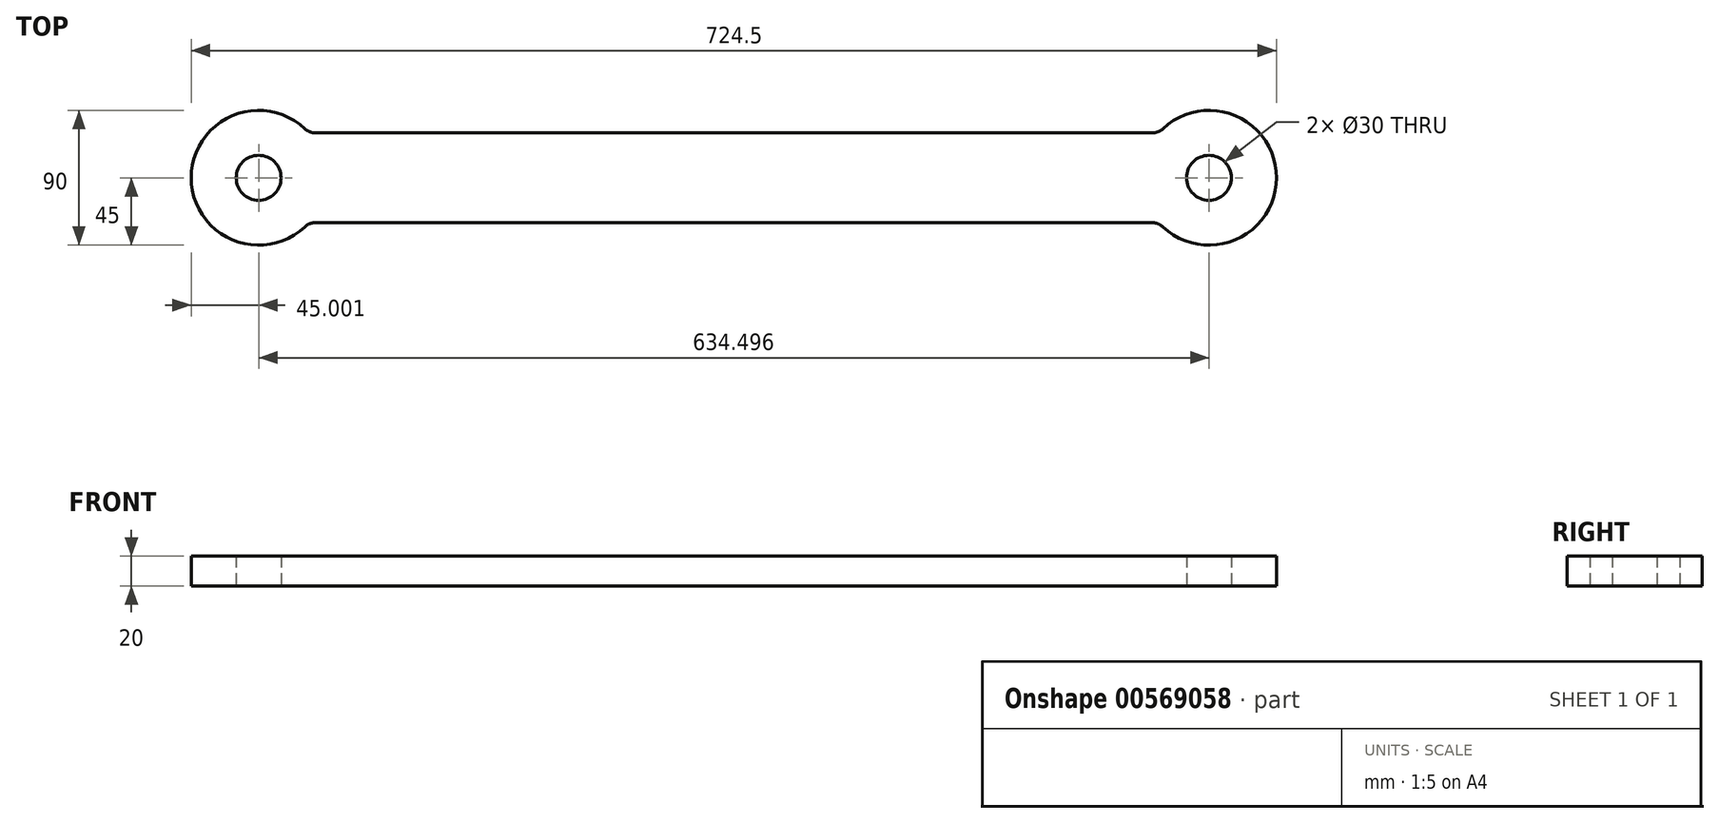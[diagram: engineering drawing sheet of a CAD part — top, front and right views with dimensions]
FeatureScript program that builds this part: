
annotation { "Feature Type Name" : "Feature", "Feature Type Description" : "" }
export const myFeature = defineFeature(function(context is Context, id is Id, definition is map)
    precondition{}
    {
        {
            var Q0;
            Q0=qCreatedBy(makeId("Top.planeOp"), FACE);
            var sketch = newSketch(context, id + "F0", { "sketchPlane" : qUnion([Q0])});
            skCircle(sketch, "E0", {"center": v(-252.36, 0) * mm, "radius": 15 * mm});
            skCircle(sketch, "E1", {"center": v(382.14, 0) * mm, "radius": 15 * mm});
            skArc(sketch, "E2", {"start": v(351.25, -32.73) * mm, "mid": v(427.14, 0) * mm, "end": v(351.25, 32.73) * mm});
            skArc(sketch, "E3", {"start": v(-221.47, 32.73) * mm, "mid": v(-297.36, 0) * mm, "end": v(-221.47, -32.73) * mm});
            skLineSegment(sketch, "E4", {"start": v(-214.6, 30) * mm, "end": v(344.39, 30) * mm});
            skLineSegment(sketch, "E5", {"start": v(-214.6, -30) * mm, "end": v(344.39, -30) * mm});
            skPoint(sketch, "E6.visualSharp", {"position": v(-218.82, 30) * mm});
            skArc(sketch, "E6.filletArc", {"start": v(-221.47, 32.73) * mm, "mid": v(-218.3, 30.7) * mm, "end": v(-214.6, 30) * mm});
            skPoint(sketch, "E7.visualSharp", {"position": v(-218.82, -30) * mm});
            skArc(sketch, "E7.filletArc", {"start": v(-214.6, -30) * mm, "mid": v(-218.3, -30.7) * mm, "end": v(-221.47, -32.73) * mm});
            skPoint(sketch, "E8.visualSharp", {"position": v(348.6, 30) * mm});
            skArc(sketch, "E8.filletArc", {"start": v(344.39, 30) * mm, "mid": v(348.08, 30.7) * mm, "end": v(351.25, 32.73) * mm});
            skPoint(sketch, "E9.visualSharp", {"position": v(348.6, -30) * mm});
            skArc(sketch, "E9.filletArc", {"start": v(351.25, -32.73) * mm, "mid": v(348.08, -30.7) * mm, "end": v(344.39, -30) * mm});
            skSolve(sketch);
        }
        {
            var Q0;
            Q0 = qSketchRegion(id + "F0", true);
            extrude(context, id + "F1", {"entities" : qUnion([Q0]), "depth" : 20 * mm, "offsetDistance" : 25 * mm});
        }
    });
